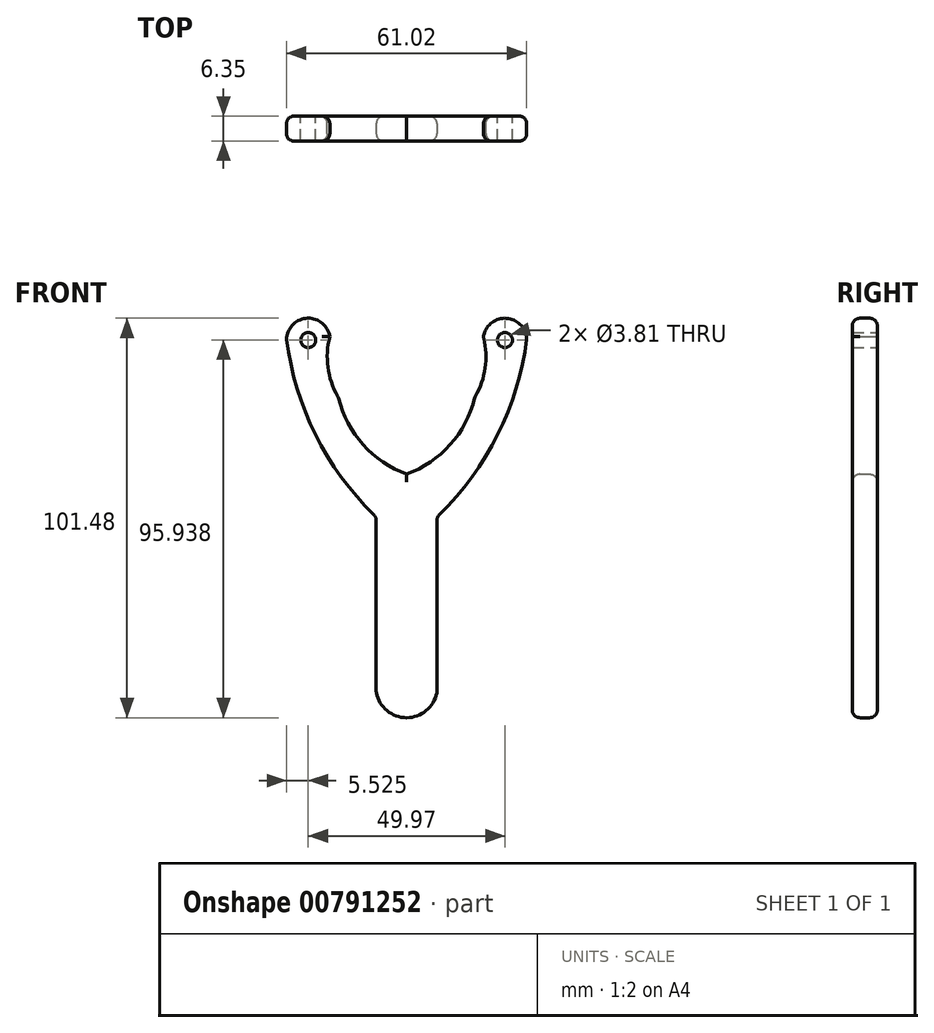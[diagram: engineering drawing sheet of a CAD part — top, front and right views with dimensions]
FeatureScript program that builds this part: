
annotation { "Feature Type Name" : "Feature", "Feature Type Description" : "" }
export const myFeature = defineFeature(function(context is Context, id is Id, definition is map)
    precondition{}
    {
        {
            var Q0;
            Q0=qCreatedBy(makeId("Front.planeOp"),FACE);
            var sketch = newSketch(context, id + "F0", { "sketchPlane" : qUnion([Q0])});
            skLineSegment(sketch, "E0", {"start": v(0, 0) * mm, "end": v(0, -44.45) * mm});
            skLineSegment(sketch, "E1", {"start": v(-7.71, 0) * mm, "end": v(0, 0) * mm});
            skLineSegment(sketch, "E2.MirrorCS", {"start": v(7.71, 0) * mm, "end": v(0, 0) * mm});
            skLineSegment(sketch, "E3", {"start": v(0, 0) * mm, "end": v(0, 50.8) * mm});
            skArc(sketch, "E4", {"start": v(-19.5, 45.82) * mm, "mid": v(-19.96, 37.95) * mm, "end": v(-17.36, 30.5) * mm});
            skLineSegment(sketch, "E5", {"start": v(0, -44.45) * mm, "end": v(0, -60.16) * mm});
            skLineSegment(sketch, "E6.MirrorCS", {"start": v(12.13, -13.7) * mm, "end": v(12.13, -13.7) * mm});
            skPoint(sketch, "E7.orphan", {"position": v(0, 50.8) * mm});
            skPoint(sketch, "E8.orphan", {"position": v(-34.92, 50.8) * mm});
            skPoint(sketch, "E9.orphan", {"position": v(34.92, 50.8) * mm});
            skPoint(sketch, "E10.end.orphan", {"position": v(-30.02, 27.43) * mm});
            skPoint(sketch, "E11.end.orphan", {"position": v(-15.1, 10.3) * mm});
            skPoint(sketch, "E12.MirrorCS.end.orphan", {"position": v(15.1, 10.3) * mm});
            skPoint(sketch, "E13.MirrorCS.end.orphan", {"position": v(30.02, 27.43) * mm});
            skArc(sketch, "E14", {"start": v(11.85, 4.28) * mm, "mid": v(24.3, 23.4) * mm, "end": v(30.52, 45.35) * mm});
            skArc(sketch, "E15.MirrorCS", {"start": v(-7.71, 0) * mm, "mid": v(-23.02, 20.7) * mm, "end": v(-30.52, 45.35) * mm});
            skArc(sketch, "E16", {"start": v(-17.36, 30.5) * mm, "mid": v(-11.14, 18.52) * mm, "end": v(0, 10.91) * mm});
            skArc(sketch, "E17.MirrorCS", {"start": v(17.36, 30.5) * mm, "mid": v(11.14, 18.52) * mm, "end": v(0, 10.91) * mm});
            skArc(sketch, "E18.trimOffspring", {"start": v(17.36, 30.5) * mm, "mid": v(19.96, 37.95) * mm, "end": v(19.5, 45.82) * mm});
            skPoint(sketch, "E19.1.internal.orphan", {"position": v(3.74, -44.45) * mm});
            skPoint(sketch, "E19.end.orphan", {"position": v(0, -51.73) * mm});
            skPoint(sketch, "E20.1.internal.orphan", {"position": v(-26.53, -41.07) * mm});
            skLineSegment(sketch, "E21.left", {"start": v(-7.71, 0) * mm, "end": v(-7.71, -44.45) * mm});
            skArc(sketch, "E22", {"start": v(-19.5, 45.82) * mm, "mid": v(-25.23, 50.53) * mm, "end": v(-30.52, 45.35) * mm});
            skArc(sketch, "E23.MirrorCS", {"start": v(19.5, 45.82) * mm, "mid": v(25.23, 50.53) * mm, "end": v(30.52, 45.35) * mm});
            skPoint(sketch, "E24.end.orphan", {"position": v(-31, 50.8) * mm});
            skPoint(sketch, "E25.orphan", {"position": v(-17.46, 50.8) * mm});
            skPoint(sketch, "E26.orphan", {"position": v(17.46, 50.8) * mm});
            skPoint(sketch, "E27.orphan", {"position": v(31, 50.8) * mm});
            skLineSegment(sketch, "E28.trimOffspring", {"start": v(-12.13, -13.7) * mm, "end": v(-12.13, -13.7) * mm});
            skArc(sketch, "E29.MirrorCS", {"start": v(7.71, 0) * mm, "mid": v(23.02, 20.7) * mm, "end": v(30.52, 45.35) * mm});
            skLineSegment(sketch, "E30", {"start": v(7.71, 0) * mm, "end": v(7.71, -44.45) * mm});
            skCircle(sketch, "E31", {"center": v(-24.98, 44.99) * mm, "radius": 1.9 * mm});
            skCircle(sketch, "E32.MirrorC", {"center": v(24.98, 44.99) * mm, "radius": 1.9 * mm});
            skLineSegment(sketch, "E33", {"start": v(7.71, -44.45) * mm, "end": v(-7.71, -44.45) * mm});
            skPoint(sketch, "E34.orphan", {"position": v(7.71, -52.94) * mm});
            skPoint(sketch, "E35.orphan", {"position": v(-7.71, -52.94) * mm});
            skArc(sketch, "E36", {"start": v(-7.71, -44.45) * mm, "mid": v(0, -50.95) * mm, "end": v(7.71, -44.45) * mm});
            skSolve(sketch);
        }
        {
            var Q0;
            Q0 = qSketchRegion(id + "F0", true);
            extrude(context, id + "F1", {"entities" : qUnion([Q0]), "depth" : 6.35 * mm, "offsetDistance" : 25.4 * mm});
        }
        {
            var Q0;
            Q0=makeQuery(id+"F1.opExtrude","CAP_EDGE",EDGE,{"disambiguationData":[OSD([sQuery(id+"F0.wireOp",EDGE,"E16")])],"isStart":false});
            var Q1;
            Q1=makeQuery(id+"F1.opExtrude","CAP_EDGE",EDGE,{"disambiguationData":[OSD([sQuery(id+"F0.wireOp",EDGE,"E17.MirrorCS")])],"isStart":false});
            var Q2;
            Q2=makeQuery(id+"F1.opExtrude","CAP_EDGE",EDGE,{"disambiguationData":[OSD([sQuery(id+"F0.wireOp",EDGE,"E4")])],"isStart":false});
            var Q3;
            Q3=makeQuery(id+"F1.opExtrude","CAP_EDGE",EDGE,{"disambiguationData":[OSD([sQuery(id+"F0.wireOp",EDGE,"E29.MirrorCS")])],"isStart":false});
            var Q4;
            Q4=makeQuery(id+"F1.opExtrude","CAP_EDGE",EDGE,{"disambiguationData":[OSD([sQuery(id+"F0.wireOp",EDGE,"E18.trimOffspring")])],"isStart":false});
            var Q5;
            Q5=makeQuery(id+"F1.opExtrude","CAP_EDGE",EDGE,{"disambiguationData":[OSD([sQuery(id+"F0.wireOp",EDGE,"E30")])],"isStart":false});
            var Q6;
            Q6=makeQuery(id+"F1.opExtrude","CAP_EDGE",EDGE,{"disambiguationData":[OSD([sQuery(id+"F0.wireOp",EDGE,"E21.left")])],"isStart":false});
            var Q7;
            Q7=makeQuery(id+"F1.opExtrude","CAP_EDGE",EDGE,{"disambiguationData":[OSD([sQuery(id+"F0.wireOp",EDGE,"E15.MirrorCS")])],"isStart":false});
            var Q8;
            Q8=makeQuery(id+"F1.opExtrude","CAP_EDGE",EDGE,{"disambiguationData":[OSD([sQuery(id+"F0.wireOp",EDGE,"qAZ9Lrzu-9FgS-uwnU-q2RP-S6eRXdEtsxUf")])],"isStart":false});
            var Q9;
            Q9=makeQuery(id+"F1.opExtrude","CAP_EDGE",EDGE,{"disambiguationData":[OSD([sQuery(id+"F0.wireOp",EDGE,"E30")])],"isStart":true});
            var Q10;
            Q10=makeQuery(id+"F1.opExtrude","CAP_EDGE",EDGE,{"disambiguationData":[OSD([sQuery(id+"F0.wireOp",EDGE,"qAZ9Lrzu-9FgS-uwnU-q2RP-S6eRXdEtsxUf")])],"isStart":true});
            var Q11;
            Q11=makeQuery(id+"F1.opExtrude","CAP_EDGE",EDGE,{"disambiguationData":[OSD([sQuery(id+"F0.wireOp",EDGE,"E21.left")])],"isStart":true});
            var Q12;
            Q12=makeQuery(id+"F1.opExtrude","CAP_EDGE",EDGE,{"disambiguationData":[OSD([sQuery(id+"F0.wireOp",EDGE,"E15.MirrorCS")])],"isStart":true});
            var Q13;
            Q13=makeQuery(id+"F1.opExtrude","SWEPT_EDGE",EDGE,{"disambiguationData":[OSD([sQuery(id+"F0.wireOp",EDGE,"E1"),sQuery(id+"F0.wireOp",EDGE,"E15.MirrorCS"),sQuery(id+"F0.wireOp",EDGE,"E21.left")])]});
            var Q14;
            Q14=makeQuery(id+"F1.opExtrude","SWEPT_EDGE",EDGE,{"disambiguationData":[OSD([sQuery(id+"F0.wireOp",EDGE,"E15.MirrorCS"),sQuery(id+"F0.wireOp",EDGE,"E22")])]});
            var Q15;
            Q15=makeQuery(id+"F1.opExtrude","SWEPT_EDGE",EDGE,{"disambiguationData":[OSD([sQuery(id+"F0.wireOp",EDGE,"E23.MirrorCS"),sQuery(id+"F0.wireOp",EDGE,"E29.MirrorCS")])]});
            var Q16;
            Q16=makeQuery(id+"F1.opExtrude","SWEPT_EDGE",EDGE,{"disambiguationData":[OSD([sQuery(id+"F0.wireOp",EDGE,"E18.trimOffspring"),sQuery(id+"F0.wireOp",EDGE,"E23.MirrorCS")])]});
            var Q17;
            Q17=makeQuery(id+"F1.opExtrude","SWEPT_EDGE",EDGE,{"disambiguationData":[OSD([sQuery(id+"F0.wireOp",EDGE,"E17.MirrorCS"),sQuery(id+"F0.wireOp",EDGE,"E18.trimOffspring")])]});
            var Q18;
            Q18=makeQuery(id+"F1.opExtrude","CAP_EDGE",EDGE,{"disambiguationData":[OSD([sQuery(id+"F0.wireOp",EDGE,"E4")])],"isStart":true});
            var Q19;
            Q19=makeQuery(id+"F1.opExtrude","CAP_EDGE",EDGE,{"disambiguationData":[OSD([sQuery(id+"F0.wireOp",EDGE,"E16")])],"isStart":true});
            var Q20;
            Q20=makeQuery(id+"F1.opExtrude","SWEPT_EDGE",EDGE,{"disambiguationData":[OSD([sQuery(id+"F0.wireOp",EDGE,"E4"),sQuery(id+"F0.wireOp",EDGE,"E16")])]});
            var Q21;
            Q21=makeQuery(id+"F1.opExtrude","CAP_EDGE",EDGE,{"disambiguationData":[OSD([sQuery(id+"F0.wireOp",EDGE,"E17.MirrorCS")])],"isStart":true});
            var Q22;
            Q22=makeQuery(id+"F1.opExtrude","CAP_EDGE",EDGE,{"disambiguationData":[OSD([sQuery(id+"F0.wireOp",EDGE,"E22")])],"isStart":false});
            var Q23;
            Q23=makeQuery(id+"F1.opExtrude","CAP_EDGE",EDGE,{"disambiguationData":[OSD([sQuery(id+"F0.wireOp",EDGE,"E23.MirrorCS")])],"isStart":false});
            var Q24;
            Q24=makeQuery(id+"F1.opExtrude","CAP_EDGE",EDGE,{"disambiguationData":[OSD([sQuery(id+"F0.wireOp",EDGE,"E22")])],"isStart":true});
            var Q25;
            Q25=makeQuery(id+"F1.opExtrude","CAP_EDGE",EDGE,{"disambiguationData":[OSD([sQuery(id+"F0.wireOp",EDGE,"E29.MirrorCS")])],"isStart":true});
            var Q26;
            Q26=makeQuery(id+"F1.opExtrude","SWEPT_EDGE",EDGE,{"disambiguationData":[OSD([sQuery(id+"F0.wireOp",EDGE,"E2.MirrorCS"),sQuery(id+"F0.wireOp",EDGE,"E29.MirrorCS"),sQuery(id+"F0.wireOp",EDGE,"E30")])]});
            var Q27;
            Q27=makeQuery(id+"F1.opExtrude","CAP_EDGE",EDGE,{"disambiguationData":[OSD([sQuery(id+"F0.wireOp",EDGE,"E18.trimOffspring")])],"isStart":true});
            var Q28;
            Q28=makeQuery(id+"F1.opExtrude","SWEPT_EDGE",EDGE,{"disambiguationData":[OSD([sQuery(id+"F0.wireOp",EDGE,"E21.left"),sQuery(id+"F0.wireOp",EDGE,"qAZ9Lrzu-9FgS-uwnU-q2RP-S6eRXdEtsxUf")])]});
            var Q29;
            Q29=makeQuery(id+"F1.opExtrude","SWEPT_EDGE",EDGE,{"disambiguationData":[OSD([sQuery(id+"F0.wireOp",EDGE,"E30"),sQuery(id+"F0.wireOp",EDGE,"qAZ9Lrzu-9FgS-uwnU-q2RP-S6eRXdEtsxUf")])]});
            var Q30;
            Q30=makeQuery(id+"F1.opExtrude","CAP_EDGE",EDGE,{"disambiguationData":[OSD([sQuery(id+"F0.wireOp",EDGE,"E36")])],"isStart":true});
            var Q31;
            Q31=makeQuery(id+"F1.opExtrude","CAP_EDGE",EDGE,{"disambiguationData":[OSD([sQuery(id+"F0.wireOp",EDGE,"E36")])],"isStart":false});
            fillet(context, id + "F2", {"entities" : qUnion([Q0, Q1, Q2, Q3, Q4, Q5, Q6, Q7, Q8, Q9, Q10, Q11, Q12, Q13, Q14, Q15, Q16, Q17, Q18, Q19, Q20, Q21, Q22, Q23, Q24, Q25, Q26, Q27, Q28, Q29, Q30, Q31]), "radius" : 1.9 * mm, "tangentPropagation" : true, "allowEdgeOverflow" : false});
        }
        {
            var Q0;
            Q0=makeQuery(id+"F1.opExtrude","CAP_EDGE",EDGE,{"disambiguationData":[OSD([sQuery(id+"F0.wireOp",EDGE,"E23.MirrorCS")])],"isStart":true});
            fillet(context, id + "F3", {"entities" : qUnion([Q0]), "radius" : 1.9 * mm, "tangentPropagation" : true, "allowEdgeOverflow" : false});
        }
    });
